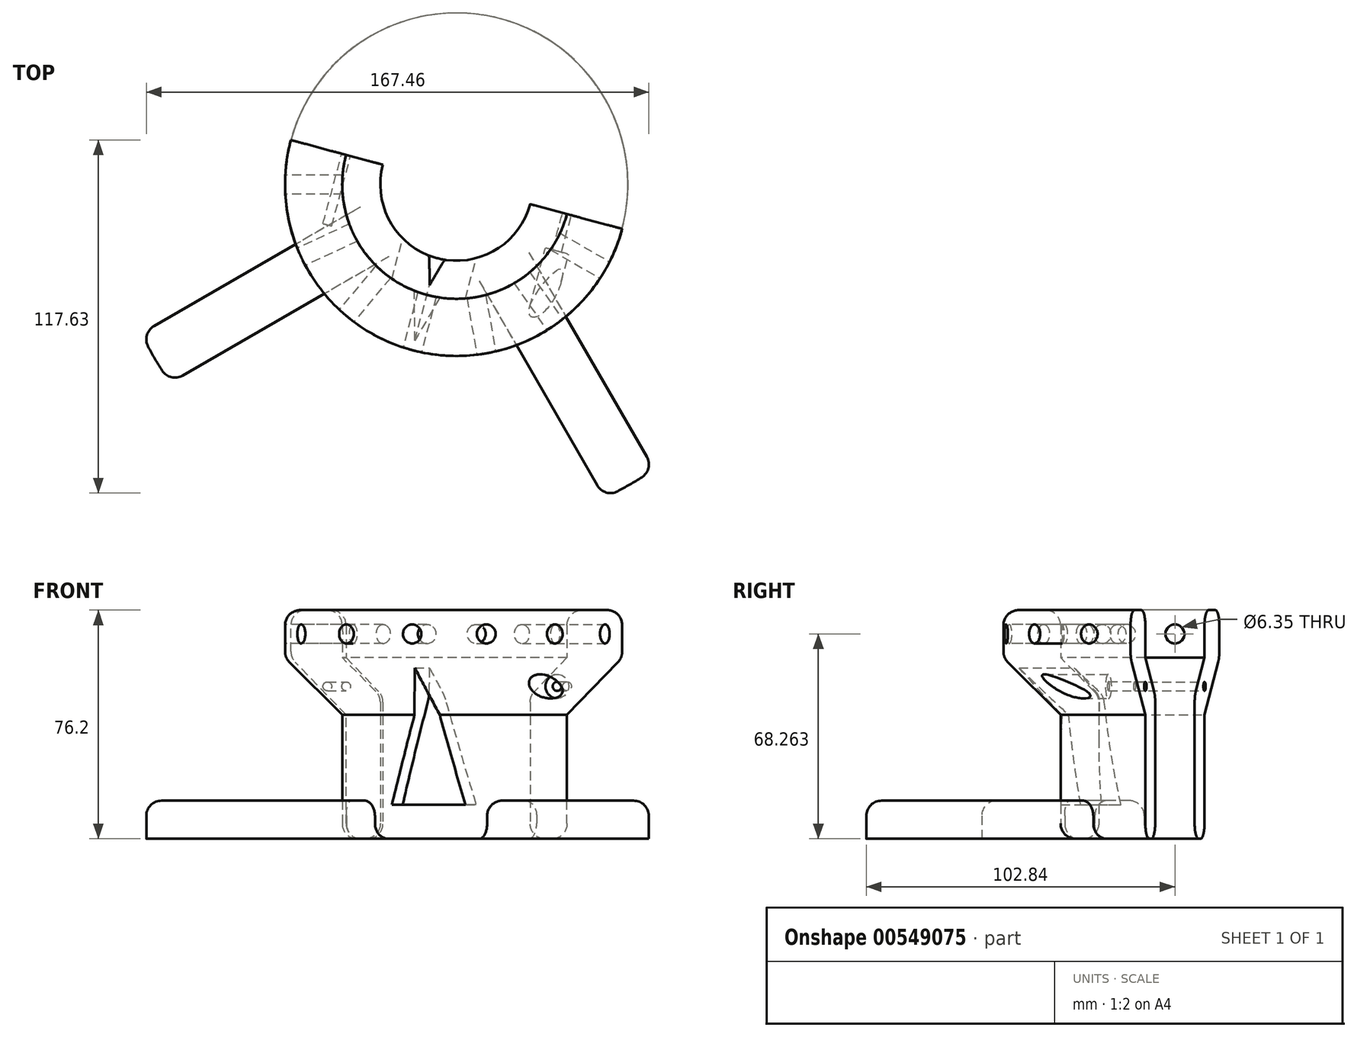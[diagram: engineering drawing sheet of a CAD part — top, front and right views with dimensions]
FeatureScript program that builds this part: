
annotation { "Feature Type Name" : "Feature", "Feature Type Description" : "" }
export const myFeature = defineFeature(function(context is Context, id is Id, definition is map)
    precondition{}
    {
        {
            var Q0;
            Q0=qCreatedBy(makeId("Top.planeOp"),FACE);
            var sketch = newSketch(context, id + "F0", { "sketchPlane" : qUnion([Q0])});
            skCircle(sketch, "E0", {"center": v(0, 0) * mm, "radius": 115.89 * mm, "construction": true});
            skSolve(sketch);
        }
        {
            var Q0;
            Q0=qCreatedBy(makeId("Front.planeOp"),FACE);
            var sketch = newSketch(context, id + "F1", { "sketchPlane" : qUnion([Q0])});
            skLineSegment(sketch, "E1", {"start": v(-25.4, 0) * mm, "end": v(-38.1, 0) * mm});
            skLineSegment(sketch, "E2", {"start": v(-38.1, 0) * mm, "end": v(-38.1, 41.28) * mm});
            skLineSegment(sketch, "E3", {"start": v(-38.1, 41.28) * mm, "end": v(-57.15, 60.33) * mm});
            skLineSegment(sketch, "E4", {"start": v(-57.15, 60.33) * mm, "end": v(-57.15, 76.2) * mm});
            skLineSegment(sketch, "E5", {"start": v(-57.15, 76.2) * mm, "end": v(-38.1, 76.2) * mm});
            skLineSegment(sketch, "E6", {"start": v(-38.1, 76.2) * mm, "end": v(-38.1, 60.33) * mm});
            skLineSegment(sketch, "E7", {"start": v(-38.1, 60.33) * mm, "end": v(-38.1, 60.33) * mm});
            skLineSegment(sketch, "E8", {"start": v(-38.1, 60.33) * mm, "end": v(-25.4, 47.62) * mm});
            skLineSegment(sketch, "E9", {"start": v(-25.4, 47.63) * mm, "end": v(-25.4, 0) * mm});
            skLineSegment(sketch, "E10", {"start": v(-38.1, 60.33) * mm, "end": v(-57.15, 60.33) * mm, "construction": true});
            skLineSegment(sketch, "E11", {"start": v(-38.1, 60.33) * mm, "end": v(-38.1, 41.28) * mm, "construction": true});
            skLineSegment(sketch, "E12", {"start": v(0, 0) * mm, "end": v(0, 85.37) * mm});
            skSolve(sketch);
        }
        {
            var Q0;
            Q0=makeQuery(id+"F1.imprint","IMPRINT",FACE,{"disambiguationData":[TD([[makeQuery(id+"F1.imprint","IMPRINT",EDGE,{"derivedFrom":sQuery(id+"F1.wireOp",EDGE,"E1")}),-1.0]])]});
            var Q1;
            Q1=sQuery(id+"F1.wireOp",EDGE,"E12");
            revolve(context, id + "F2", {"entities" : qUnion([Q0]), "axis" : qUnion([Q1]), "revolveType" : RevolveType.SYMMETRIC, "angle" : 30 * degree});
        }
        {
            var Q0;
            Q0=qCreatedBy(makeId("Right.planeOp"),FACE);
            cPlane(context, id + "F3", {"entities" : qUnion([Q0]), "cplaneType" : CPlaneType.OFFSET, "offset" : 57.15 * mm, "oppositeDirection" : true, "width" : 152.4 * mm, "height" : 152.4 * mm});
        }
        {
            var Q0;
            Q0=qCreatedBy(id+"F3.planeOp",FACE);
            var sketch = newSketch(context, id + "F4", { "sketchPlane" : qUnion([Q0])});
            skPoint(sketch, "E13", {"position": v(0, 68.26) * mm});
            skCircle(sketch, "E14", {"center": v(0, 68.26) * mm, "radius": 3.18 * mm});
            skSolve(sketch);
        }
        {
            var Q0;
            Q0 = qSketchRegion(id + "F4", true);
            extrude(context, id + "F5", {"entities" : qUnion([Q0]), "operationType" : NewBodyOperationType.REMOVE, "depth" : 50.8 * mm, "offsetDistance" : 25.4 * mm});
        }
        {
            var Q0;
            Q0=makeQuery(id+"F2.opRevolve","SWEPT_BODY",BODY,{"disambiguationData":[OSD([sQuery(id+"F1.wireOp",EDGE,"E1"),sQuery(id+"F1.wireOp",EDGE,"E2"),sQuery(id+"F1.wireOp",EDGE,"E3"),sQuery(id+"F1.wireOp",EDGE,"E4"),sQuery(id+"F1.wireOp",EDGE,"E5"),sQuery(id+"F1.wireOp",EDGE,"E6"),sQuery(id+"F1.wireOp",EDGE,"E8"),sQuery(id+"F1.wireOp",EDGE,"E9")])]});
            var Q1;
            Q1=makeQuery(id+"F2.opRevolve","SWEPT_FACE",FACE,{"disambiguationData":[OSD([sQuery(id+"F1.wireOp",EDGE,"E9")])]});
            circularPattern(context, id + "F6", {"operationType" : NewBodyOperationType.ADD, "entities" : qUnion([Q0]), "axis" : qUnion([Q1]), "angle" : 150 * degree, "instanceCount" : 7, "equalSpace" : true});
        }
        {
            var Q0;
            Q0=qCreatedBy(makeId("Top.planeOp"),FACE);
            var sketch = newSketch(context, id + "F7", { "sketchPlane" : qUnion([Q0])});
            skArc(sketch, "E15.0", {"start": v(36.8, -9.86) * mm, "mid": v(-9.86, -36.8) * mm, "end": v(-36.8, 9.86) * mm});
            skLineSegment(sketch, "E16", {"start": v(0, 0) * mm, "end": v(-29.75, -111.04) * mm, "construction": true});
            skLineSegment(sketch, "E17", {"start": v(0, 0) * mm, "end": v(57.74, -100) * mm, "construction": true});
            skCircle(sketch, "E18.0", {"center": v(-0.38, 0.26) * mm, "radius": 115.89 * mm});
            skLineSegment(sketch, "E19", {"start": v(10.2, -36.71) * mm, "end": v(49.3, -104.44) * mm});
            skLineSegment(sketch, "E20", {"start": v(26.7, -27.19) * mm, "end": v(65.78, -94.89) * mm});
            skLineSegment(sketch, "E21", {"start": v(0, 0) * mm, "end": v(-100.54, -58.05) * mm, "construction": true});
            skLineSegment(sketch, "E22", {"start": v(-27.19, -26.7) * mm, "end": v(-95.4, -66.08) * mm});
            skLineSegment(sketch, "E23", {"start": v(-36.71, -10.2) * mm, "end": v(-104.99, -49.62) * mm});
            skSolve(sketch);
        }
        {
            var Q0;
            {var subQ0=sQuery(id+"F7.wireOp",EDGE,"E22");Q0=makeQuery(id+"F7.imprint","IMPRINT",FACE,{"disambiguationData":[TD([[makeQuery(id+"F7.imprint","IMPRINT",EDGE,{"derivedFrom":subQ0}),-1.0]])]});}
            var Q1;
            {var subQ0=sQuery(id+"F7.wireOp",EDGE,"E19");Q1=makeQuery(id+"F7.imprint","IMPRINT",FACE,{"disambiguationData":[TD([[makeQuery(id+"F7.imprint","IMPRINT",EDGE,{"derivedFrom":subQ0}),1.0]])]});}
            extrude(context, id + "F8", {"entities" : qUnion([Q0, Q1]), "operationType" : NewBodyOperationType.ADD, "depth" : 12.7 * mm, "offsetDistance" : 25.4 * mm});
        }
        {
            var Q0;
            Q0=makeQuery(id+"F6.opPattern","COPY",FACE,{"derivedFrom":makeQuery(id+"F2.opRevolve","CAP_FACE",FACE,{"disambiguationData":[OSD([sQuery(id+"F1.wireOp",EDGE,"E1"),sQuery(id+"F1.wireOp",EDGE,"E2"),sQuery(id+"F1.wireOp",EDGE,"E3"),sQuery(id+"F1.wireOp",EDGE,"E4"),sQuery(id+"F1.wireOp",EDGE,"E5"),sQuery(id+"F1.wireOp",EDGE,"E6"),sQuery(id+"F1.wireOp",EDGE,"E8"),sQuery(id+"F1.wireOp",EDGE,"E9")])],"isStart":false}),"instanceName":"6"});
            var sketch = newSketch(context, id + "F9", { "sketchPlane" : qUnion([Q0])});
            skPoint(sketch, "E24", {"position": v(-38.1, 50.8) * mm});
            skPoint(sketch, "E25", {"position": v(38.1, 50.8) * mm});
            skCircle(sketch, "E26", {"center": v(-38.1, 50.8) * mm, "radius": 1.52 * mm});
            skCircle(sketch, "E27", {"center": v(38.1, 50.8) * mm, "radius": 1.5 * mm});
            skSolve(sketch);
        }
        {
            var Q0;
            Q0 = qSketchRegion(id + "F9", true);
            extrude(context, id + "F10", {"entities" : qUnion([Q0]), "operationType" : NewBodyOperationType.REMOVE, "oppositeDirection" : true, "depth" : 24.13 * mm, "offsetDistance" : 25.4 * mm});
        }
        {
            var Q0;
            Q0=makeQuery(id+"F6.opPattern","COPY",FACE,{"derivedFrom":makeQuery(id+"F2.opRevolve","CAP_FACE",FACE,{"disambiguationData":[OSD([sQuery(id+"F1.wireOp",EDGE,"E1"),sQuery(id+"F1.wireOp",EDGE,"E2"),sQuery(id+"F1.wireOp",EDGE,"E3"),sQuery(id+"F1.wireOp",EDGE,"E4"),sQuery(id+"F1.wireOp",EDGE,"E5"),sQuery(id+"F1.wireOp",EDGE,"E6"),sQuery(id+"F1.wireOp",EDGE,"E8"),sQuery(id+"F1.wireOp",EDGE,"E9")])],"isStart":false}),"instanceName":"6"});
            cPlane(context, id + "F11", {"entities" : qUnion([Q0]), "cplaneType" : CPlaneType.OFFSET, "offset" : 12.7 * mm, "oppositeDirection" : true, "width" : 152.4 * mm, "height" : 152.4 * mm});
        }
        {
            var Q0;
            Q0=qCreatedBy(id+"F11.planeOp",FACE);
            var sketch = newSketch(context, id + "F12", { "sketchPlane" : qUnion([Q0])});
            skCircle(sketch, "E28.0", {"center": v(-38.1, 50.8) * mm, "radius": 1.52 * mm});
            skCircle(sketch, "E29.0", {"center": v(38.1, 50.8) * mm, "radius": 1.5 * mm});
            skCircle(sketch, "E30", {"center": v(-38.1, 50.8) * mm, "radius": 4 * mm});
            skCircle(sketch, "E31", {"center": v(38.1, 50.8) * mm, "radius": 4 * mm});
            skSolve(sketch);
        }
        {
            var Q0;
            Q0=makeQuery(id+"F12.imprint","IMPRINT",FACE,{"disambiguationData":[TD([[makeQuery(id+"F12.imprint","IMPRINT",EDGE,{"derivedFrom":sQuery(id+"F12.wireOp",EDGE,"E28.0")}),-1.0]])]});
            var Q1;
            Q1=makeQuery(id+"F12.imprint","IMPRINT",FACE,{"disambiguationData":[TD([[makeQuery(id+"F12.imprint","IMPRINT",EDGE,{"derivedFrom":sQuery(id+"F12.wireOp",EDGE,"E28.0")}),1.0]])]});
            extrude(context, id + "F13", {"entities" : qUnion([Q0, Q1]), "operationType" : NewBodyOperationType.REMOVE, "oppositeDirection" : true, "depth" : 38.1 * mm, "offsetDistance" : 25.4 * mm});
        }
        {
            var Q0;
            {var subQ0=sQuery(id+"F7.wireOp",EDGE,"E15.0");Q0=makeQuery(id+"F8.opExtrude","CAP_EDGE",EDGE,{"disambiguationData":[OSD([subQ0]),TDD([makeQuery(id+"F7.imprint","IMPRINT",EDGE,{"disambiguationData":[TD([[makeQuery(id+"F7.imprint","INTERSECT",VERTEX,{"derivedFrom":[subQ0,sQuery(id+"F7.wireOp",EDGE,"E22")]}),-1.0]])],"derivedFrom":subQ0})])],"isStart":false});}
            var Q1;
            Q1=makeQuery(id+"F8.opExtrude","SWEPT_EDGE",EDGE,{"disambiguationData":[OSD([sQuery(id+"F7.wireOp",EDGE,"E15.0"),sQuery(id+"F7.wireOp",EDGE,"E22")])]});
            var Q2;
            Q2=makeQuery(id+"F8.opExtrude","SWEPT_EDGE",EDGE,{"disambiguationData":[OSD([sQuery(id+"F7.wireOp",EDGE,"E15.0"),sQuery(id+"F7.wireOp",EDGE,"E19")])]});
            var Q3;
            {var subQ0=sQuery(id+"F7.wireOp",EDGE,"E15.0");Q3=makeQuery(id+"F8.opExtrude","CAP_EDGE",EDGE,{"disambiguationData":[OSD([subQ0]),TDD([makeQuery(id+"F7.imprint","IMPRINT",EDGE,{"disambiguationData":[TD([[makeQuery(id+"F7.imprint","INTERSECT",VERTEX,{"derivedFrom":[subQ0,sQuery(id+"F7.wireOp",EDGE,"E19")]}),1.0]])],"derivedFrom":subQ0})])],"isStart":false});}
            var Q4;
            Q4=makeQuery(id+"F8.opExtrude","SWEPT_EDGE",EDGE,{"disambiguationData":[OSD([sQuery(id+"F7.wireOp",EDGE,"E15.0"),sQuery(id+"F7.wireOp",EDGE,"E23")])]});
            var Q5;
            Q5=makeQuery(id+"F8.opExtrude","SWEPT_EDGE",EDGE,{"disambiguationData":[OSD([sQuery(id+"F7.wireOp",EDGE,"E15.0"),sQuery(id+"F7.wireOp",EDGE,"E20")])]});
            var Q6;
            {var subQ0=makeQuery(id+"F2.opRevolve","SWEPT_EDGE",EDGE,{"disambiguationData":[OSD([sQuery(id+"F1.wireOp",EDGE,"E3"),sQuery(id+"F1.wireOp",EDGE,"E4")])]});Q6=makeQuery(id+"F6.boolean.opBoolean","MERGE",EDGE,{"derivedFrom":[subQ0,makeQuery(id+"F6.opPattern","COPY",EDGE,{"derivedFrom":subQ0,"instanceName":"1"}),makeQuery(id+"F6.opPattern","COPY",EDGE,{"derivedFrom":subQ0,"instanceName":"2"}),makeQuery(id+"F6.opPattern","COPY",EDGE,{"derivedFrom":subQ0,"instanceName":"3"}),makeQuery(id+"F6.opPattern","COPY",EDGE,{"derivedFrom":subQ0,"instanceName":"4"}),makeQuery(id+"F6.opPattern","COPY",EDGE,{"derivedFrom":subQ0,"instanceName":"5"}),makeQuery(id+"F6.opPattern","COPY",EDGE,{"derivedFrom":subQ0,"instanceName":"6"})]});}
            var Q7;
            {var subQ0=makeQuery(id+"F2.opRevolve","SWEPT_EDGE",EDGE,{"disambiguationData":[OSD([sQuery(id+"F1.wireOp",EDGE,"E4"),sQuery(id+"F1.wireOp",EDGE,"E5")])]});Q7=makeQuery(id+"F6.boolean.opBoolean","MERGE",EDGE,{"derivedFrom":[subQ0,makeQuery(id+"F6.opPattern","COPY",EDGE,{"derivedFrom":subQ0,"instanceName":"1"}),makeQuery(id+"F6.opPattern","COPY",EDGE,{"derivedFrom":subQ0,"instanceName":"2"}),makeQuery(id+"F6.opPattern","COPY",EDGE,{"derivedFrom":subQ0,"instanceName":"3"}),makeQuery(id+"F6.opPattern","COPY",EDGE,{"derivedFrom":subQ0,"instanceName":"4"}),makeQuery(id+"F6.opPattern","COPY",EDGE,{"derivedFrom":subQ0,"instanceName":"5"}),makeQuery(id+"F6.opPattern","COPY",EDGE,{"derivedFrom":subQ0,"instanceName":"6"})]});}
            var Q8;
            {var subQ0=makeQuery(id+"F2.opRevolve","SWEPT_EDGE",EDGE,{"disambiguationData":[OSD([sQuery(id+"F1.wireOp",EDGE,"E5"),sQuery(id+"F1.wireOp",EDGE,"E6")])]});Q8=makeQuery(id+"F6.boolean.opBoolean","MERGE",EDGE,{"derivedFrom":[subQ0,makeQuery(id+"F6.opPattern","COPY",EDGE,{"derivedFrom":subQ0,"instanceName":"1"}),makeQuery(id+"F6.opPattern","COPY",EDGE,{"derivedFrom":subQ0,"instanceName":"2"}),makeQuery(id+"F6.opPattern","COPY",EDGE,{"derivedFrom":subQ0,"instanceName":"3"}),makeQuery(id+"F6.opPattern","COPY",EDGE,{"derivedFrom":subQ0,"instanceName":"4"}),makeQuery(id+"F6.opPattern","COPY",EDGE,{"derivedFrom":subQ0,"instanceName":"5"}),makeQuery(id+"F6.opPattern","COPY",EDGE,{"derivedFrom":subQ0,"instanceName":"6"})]});}
            fillet(context, id + "F14", {"entities" : qUnion([Q0, Q1, Q2, Q3, Q4, Q5, Q6, Q7, Q8]), "radius" : 5.08 * mm, "tangentPropagation" : true, "allowEdgeOverflow" : false});
        }
        {
            var Q0;
            Q0=makeQuery(id+"F8.opExtrude","CAP_EDGE",EDGE,{"disambiguationData":[OSD([sQuery(id+"F7.wireOp",EDGE,"E23")])],"isStart":false});
            var Q1;
            {var subQ0=sQuery(id+"F7.wireOp",EDGE,"E18.0");Q1=makeQuery(id+"F8.opExtrude","CAP_EDGE",EDGE,{"disambiguationData":[OSD([subQ0]),TDD([makeQuery(id+"F7.imprint","IMPRINT",EDGE,{"disambiguationData":[TD([[makeQuery(id+"F7.imprint","INTERSECT",VERTEX,{"derivedFrom":[subQ0,sQuery(id+"F7.wireOp",EDGE,"E22")]}),1.0]])],"derivedFrom":subQ0})])],"isStart":false});}
            var Q2;
            Q2=makeQuery(id+"F8.opExtrude","CAP_EDGE",EDGE,{"disambiguationData":[OSD([sQuery(id+"F7.wireOp",EDGE,"E22")])],"isStart":false});
            var Q3;
            Q3=makeQuery(id+"F8.opExtrude","SWEPT_EDGE",EDGE,{"disambiguationData":[OSD([sQuery(id+"F7.wireOp",EDGE,"E18.0"),sQuery(id+"F7.wireOp",EDGE,"E23")])]});
            var Q4;
            Q4=makeQuery(id+"F8.opExtrude","SWEPT_EDGE",EDGE,{"disambiguationData":[OSD([sQuery(id+"F7.wireOp",EDGE,"E18.0"),sQuery(id+"F7.wireOp",EDGE,"E22")])]});
            var Q5;
            Q5=makeQuery(id+"F8.opExtrude","CAP_EDGE",EDGE,{"disambiguationData":[OSD([sQuery(id+"F7.wireOp",EDGE,"E19")])],"isStart":false});
            var Q6;
            {var subQ0=sQuery(id+"F7.wireOp",EDGE,"E18.0");Q6=makeQuery(id+"F8.opExtrude","CAP_EDGE",EDGE,{"disambiguationData":[OSD([subQ0]),TDD([makeQuery(id+"F7.imprint","IMPRINT",EDGE,{"disambiguationData":[TD([[makeQuery(id+"F7.imprint","INTERSECT",VERTEX,{"derivedFrom":[subQ0,sQuery(id+"F7.wireOp",EDGE,"E19")]}),-1.0]])],"derivedFrom":subQ0})])],"isStart":false});}
            var Q7;
            Q7=makeQuery(id+"F8.opExtrude","CAP_EDGE",EDGE,{"disambiguationData":[OSD([sQuery(id+"F7.wireOp",EDGE,"E20")])],"isStart":false});
            var Q8;
            {var subQ0=makeQuery(id+"F2.opRevolve","SWEPT_EDGE",EDGE,{"disambiguationData":[OSD([sQuery(id+"F1.wireOp",EDGE,"E8"),sQuery(id+"F1.wireOp",EDGE,"E9")])]});Q8=makeQuery(id+"F6.boolean.opBoolean","MERGE",EDGE,{"derivedFrom":[subQ0,makeQuery(id+"F6.opPattern","COPY",EDGE,{"derivedFrom":subQ0,"instanceName":"1"}),makeQuery(id+"F6.opPattern","COPY",EDGE,{"derivedFrom":subQ0,"instanceName":"2"}),makeQuery(id+"F6.opPattern","COPY",EDGE,{"derivedFrom":subQ0,"instanceName":"3"}),makeQuery(id+"F6.opPattern","COPY",EDGE,{"derivedFrom":subQ0,"instanceName":"4"}),makeQuery(id+"F6.opPattern","COPY",EDGE,{"derivedFrom":subQ0,"instanceName":"5"}),makeQuery(id+"F6.opPattern","COPY",EDGE,{"derivedFrom":subQ0,"instanceName":"6"})]});}
            var Q9;
            {var subQ0=makeQuery(id+"F2.opRevolve","SWEPT_EDGE",EDGE,{"disambiguationData":[OSD([sQuery(id+"F1.wireOp",EDGE,"E1"),sQuery(id+"F1.wireOp",EDGE,"E9")])]});Q9=makeQuery(id+"F6.boolean.opBoolean","MERGE",EDGE,{"derivedFrom":[subQ0,makeQuery(id+"F6.opPattern","COPY",EDGE,{"derivedFrom":subQ0,"instanceName":"1"}),makeQuery(id+"F6.opPattern","COPY",EDGE,{"derivedFrom":subQ0,"instanceName":"2"}),makeQuery(id+"F6.opPattern","COPY",EDGE,{"derivedFrom":subQ0,"instanceName":"3"}),makeQuery(id+"F6.opPattern","COPY",EDGE,{"derivedFrom":subQ0,"instanceName":"4"}),makeQuery(id+"F6.opPattern","COPY",EDGE,{"derivedFrom":subQ0,"instanceName":"5"}),makeQuery(id+"F6.opPattern","COPY",EDGE,{"derivedFrom":subQ0,"instanceName":"6"})]});}
            var Q10;
            {var subQ0=sQuery(id+"F1.wireOp",EDGE,"E1");var subQ2=sQuery(id+"F1.wireOp",EDGE,"E2");var subQ5=sQuery(id+"F7.wireOp",EDGE,"E19");var subQ8=makeQuery(id+"F2.opRevolve","SWEPT_EDGE",EDGE,{"disambiguationData":[OSD([subQ0,subQ2])]});Q10=makeQuery(id+"F8.boolean.opBoolean","SPLIT",EDGE,{"disambiguationData":[TD([makeQuery(id+"F8.opExtrude","SWEPT_FACE",FACE,{"disambiguationData":[OSD([subQ5])]})])],"derivedFrom":makeQuery(id+"F6.boolean.opBoolean","MERGE",EDGE,{"derivedFrom":[subQ8,makeQuery(id+"F6.opPattern","COPY",EDGE,{"derivedFrom":subQ8,"instanceName":"1"}),makeQuery(id+"F6.opPattern","COPY",EDGE,{"derivedFrom":subQ8,"instanceName":"2"}),makeQuery(id+"F6.opPattern","COPY",EDGE,{"derivedFrom":subQ8,"instanceName":"3"}),makeQuery(id+"F6.opPattern","COPY",EDGE,{"derivedFrom":subQ8,"instanceName":"4"}),makeQuery(id+"F6.opPattern","COPY",EDGE,{"derivedFrom":subQ8,"instanceName":"5"}),makeQuery(id+"F6.opPattern","COPY",EDGE,{"derivedFrom":subQ8,"instanceName":"6"})]})});}
            var Q11;
            {var subQ0=sQuery(id+"F1.wireOp",EDGE,"E1");var subQ2=sQuery(id+"F1.wireOp",EDGE,"E2");var subQ4=sQuery(id+"F7.wireOp",EDGE,"E20");var subQ7=makeQuery(id+"F2.opRevolve","SWEPT_EDGE",EDGE,{"disambiguationData":[OSD([subQ0,subQ2])]});Q11=makeQuery(id+"F8.boolean.opBoolean","SPLIT",EDGE,{"disambiguationData":[TD([makeQuery(id+"F8.opExtrude","SWEPT_FACE",FACE,{"disambiguationData":[OSD([subQ4])]})])],"derivedFrom":makeQuery(id+"F6.boolean.opBoolean","MERGE",EDGE,{"derivedFrom":[subQ7,makeQuery(id+"F6.opPattern","COPY",EDGE,{"derivedFrom":subQ7,"instanceName":"1"}),makeQuery(id+"F6.opPattern","COPY",EDGE,{"derivedFrom":subQ7,"instanceName":"2"}),makeQuery(id+"F6.opPattern","COPY",EDGE,{"derivedFrom":subQ7,"instanceName":"3"}),makeQuery(id+"F6.opPattern","COPY",EDGE,{"derivedFrom":subQ7,"instanceName":"4"}),makeQuery(id+"F6.opPattern","COPY",EDGE,{"derivedFrom":subQ7,"instanceName":"5"}),makeQuery(id+"F6.opPattern","COPY",EDGE,{"derivedFrom":subQ7,"instanceName":"6"})]})});}
            var Q12;
            {var subQ0=sQuery(id+"F1.wireOp",EDGE,"E2");var subQ4=sQuery(id+"F1.wireOp",EDGE,"E1");var subQ6=sQuery(id+"F7.wireOp",EDGE,"E23");var subQ7=makeQuery(id+"F2.opRevolve","SWEPT_EDGE",EDGE,{"disambiguationData":[OSD([subQ4,subQ0])]});Q12=makeQuery(id+"F8.boolean.opBoolean","SPLIT",EDGE,{"disambiguationData":[TD([makeQuery(id+"F8.opExtrude","SWEPT_FACE",FACE,{"disambiguationData":[OSD([subQ6])]})])],"derivedFrom":makeQuery(id+"F6.boolean.opBoolean","MERGE",EDGE,{"derivedFrom":[subQ7,makeQuery(id+"F6.opPattern","COPY",EDGE,{"derivedFrom":subQ7,"instanceName":"1"}),makeQuery(id+"F6.opPattern","COPY",EDGE,{"derivedFrom":subQ7,"instanceName":"2"}),makeQuery(id+"F6.opPattern","COPY",EDGE,{"derivedFrom":subQ7,"instanceName":"3"}),makeQuery(id+"F6.opPattern","COPY",EDGE,{"derivedFrom":subQ7,"instanceName":"4"}),makeQuery(id+"F6.opPattern","COPY",EDGE,{"derivedFrom":subQ7,"instanceName":"5"}),makeQuery(id+"F6.opPattern","COPY",EDGE,{"derivedFrom":subQ7,"instanceName":"6"})]})});}
            var Q13;
            Q13=makeQuery(id+"F8.opExtrude","SWEPT_EDGE",EDGE,{"disambiguationData":[OSD([sQuery(id+"F7.wireOp",EDGE,"E18.0"),sQuery(id+"F7.wireOp",EDGE,"E19")])]});
            var Q14;
            Q14=makeQuery(id+"F8.opExtrude","SWEPT_EDGE",EDGE,{"disambiguationData":[OSD([sQuery(id+"F7.wireOp",EDGE,"E18.0"),sQuery(id+"F7.wireOp",EDGE,"E20")])]});
            fillet(context, id + "F15", {"entities" : qUnion([Q0, Q1, Q2, Q3, Q4, Q5, Q6, Q7, Q8, Q9, Q10, Q11, Q12, Q13, Q14]), "radius" : 5.08 * mm, "tangentPropagation" : true, "allowEdgeOverflow" : false});
        }
        {
            var Q0;
            Q0=makeQuery(id+"F6.opPattern","COPY",FACE,{"derivedFrom":makeQuery(id+"F2.opRevolve","CAP_FACE",FACE,{"disambiguationData":[OSD([sQuery(id+"F1.wireOp",EDGE,"E1"),sQuery(id+"F1.wireOp",EDGE,"E2"),sQuery(id+"F1.wireOp",EDGE,"E3"),sQuery(id+"F1.wireOp",EDGE,"E4"),sQuery(id+"F1.wireOp",EDGE,"E5"),sQuery(id+"F1.wireOp",EDGE,"E6"),sQuery(id+"F1.wireOp",EDGE,"E8"),sQuery(id+"F1.wireOp",EDGE,"E9")])],"isStart":false}),"instanceName":"6"});
            var sketch = newSketch(context, id + "F16", { "sketchPlane" : qUnion([Q0])});
            skLineSegment(sketch, "E32", {"start": v(-12.7, 11.3) * mm, "end": v(12.7, 11.3) * mm});
            skLineSegment(sketch, "E33", {"start": v(12.7, 11.3) * mm, "end": v(0, 56.95) * mm});
            skLineSegment(sketch, "E34", {"start": v(0, 56.95) * mm, "end": v(-12.7, 11.3) * mm});
            skSolve(sketch);
        }
        {
            var Q0;
            Q0 = qSketchRegion(id + "F16", true);
            extrude(context, id + "F17", {"entities" : qUnion([Q0]), "operationType" : NewBodyOperationType.REMOVE, "oppositeDirection" : true, "depth" : 76.2 * mm, "offsetDistance" : 25.4 * mm});
        }
    });
